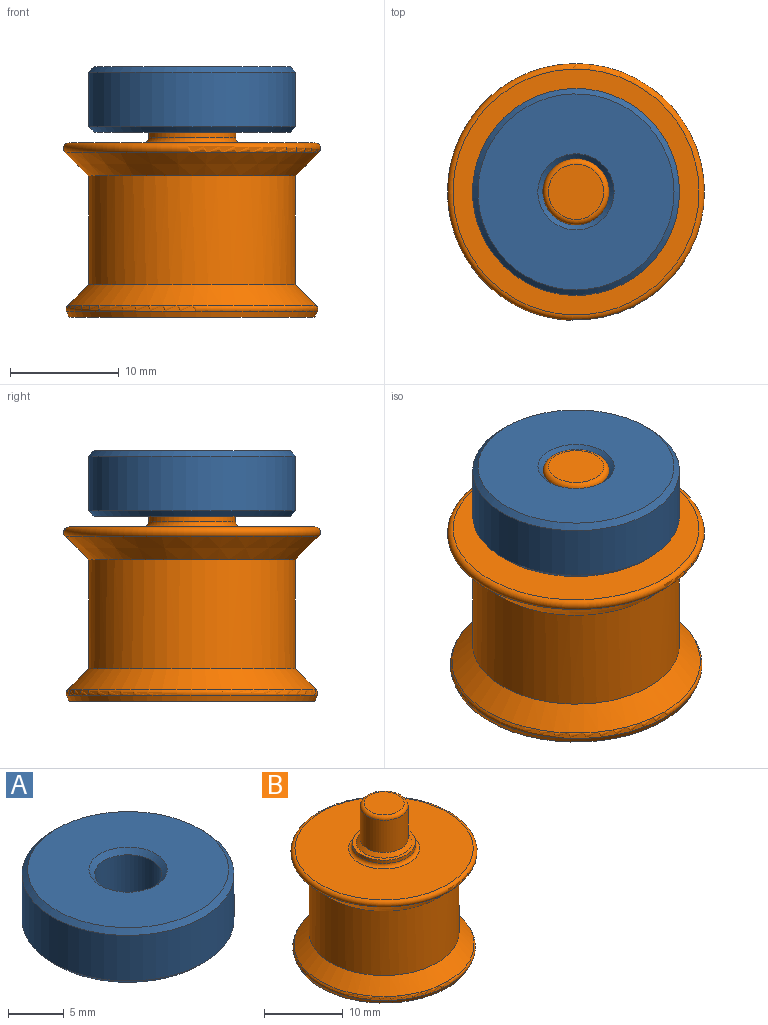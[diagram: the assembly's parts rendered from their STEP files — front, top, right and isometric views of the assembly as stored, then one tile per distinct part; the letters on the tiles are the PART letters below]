
ASSEMBLY  parts=2 mates=1
PART A: 8 faces, bbox 19x19x6 mm
  f0: cylinder r=3mm len=6mm, axis (0,0,-1), area 94.2mm2, adj f4,f6
  f1: cylinder r=9.5mm len=19mm, axis (0,0,-1), area 298.5mm2, adj f5,f7
  f2: plane 18x18mm, normal (0,0,1), area 216mm2, adj f6,f7
  f3: plane 18x18mm, normal (0,0,-1), area 216mm2, adj f4,f5
  f4: cone r=3.5mm half-angle=45deg, axis (0,0,-1), area 14.4mm2, adj f0,f3
  f5: cone r=9.5mm half-angle=45deg, axis (0,0,1), area 41.1mm2, adj f1,f3
  f6: cone r=3mm half-angle=45deg, axis (0,0,1), area 14.4mm2, adj f0,f2
  f7: cone r=9mm half-angle=45deg, axis (0,0,-1), area 41.1mm2, adj f1,f2
PART B: 19 faces, bbox 25.5x25.5x23 mm
  f0: cylinder r=4mm len=8mm, axis (0,0,-1), area 12.6mm2, adj f1,f16
  f1: plane 8x8mm, normal (0,0,1), area 11mm2, adj f0,f14
  f2: cylinder r=3.04mm len=6.08mm, axis (0,0,-1), area 95.4mm2, adj f14,f18
  f3: plane 5.08x5.08mm, normal (0,0,1), area 20.2mm2, adj f18
  f4: cone r=12.5mm half-angle=45deg, axis (0,0,1), area 201.7mm2, adj f6,f17
  f5: plane 22.59x22.59mm, normal (0,0,1), area 337mm2, adj f16,f17
  f6: cylinder r=9.5mm len=19mm, axis (0,0,1), area 596.9mm2, adj f4,f7
  f7: cone r=9.5mm half-angle=45deg, axis (0,0,-1), area 177.5mm2, adj f6,f15
  f8: plane 22.59x22.59mm, normal (0,0,-1), area 246.7mm2, adj f11,f13
  f9: cylinder r=6.5mm len=13mm, axis (0,0,-1), area 490.1mm2, adj f12,f13
  f10: plane 12x12mm, normal (0,0,-1), area 113.1mm2, adj f12
  f11: cone r=11.65mm half-angle=22.5deg, axis (0,0,1), area 42.3mm2, adj f8,f15
  f12: cone r=6mm half-angle=45deg, axis (0,0,-1), area 27.8mm2, adj f9,f10
  f13: cone r=6.5mm half-angle=45deg, axis (0,0,-1), area 30mm2, adj f8,f9
  f14: cone r=3.04mm half-angle=45deg, axis (0,0,-1), area 14.6mm2, adj f1,f2
  f15: torus R=11.06mm, axis (0,0,-1), area 42.6mm2, adj f7,f11
  f16: torus R=4.5mm, axis (0,0,1), area 20.6mm2, adj f0,f5
  f17: torus R=11.29mm, axis (0,0,1), area 86.3mm2, adj f4,f5
  f18: torus R=2.54mm, axis (0,0,1), area 14.1mm2, adj f2,f3
PLACE A t=(-8.16,2.63,23.01)mm
PLACE B t=(-8.16,2.63,22.01)mm
MATE fastened A.f0 <-> B.f2  axis (0,0,1) through (-8.16,2.63,29.01)mm
